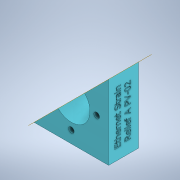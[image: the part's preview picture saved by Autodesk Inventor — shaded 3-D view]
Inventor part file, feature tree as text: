
AUTODESK INVENTOR PART (.ipt)
format: ipt  version: 2022.1 (Build 261234000, 234)  size: 969,216 bytes
history: native  units: mm
features: sketch x7, extrude x2, revolve x2, emboss x2, hole x1, plane x1, split x1
ambient origin geometry x8: Origin, YZ Plane, XZ Plane, XY Plane, X Axis, Y Axis, Z Axis, Center Point
bodies: Solid7 (feature_tree)
feature tree (16):
  extrude  "Extrusion20"  Depth=50.0mm
  revolve  "Revolution4"  [1 undecoded]
  extrude  "Extrusion21"  TaperAngle=90.0deg  [1 undecoded]
  revolve  "Revolution5"  [1 undecoded]
  hole  "Hole2"  [1 undecoded]
  plane  "Work Plane6"
  emboss  "Emboss3"
  emboss  "Emboss4"
  split  "Split1"
  sketch  "Sketch27"  dims[d124=50.0mm d125=50.0mm]
  sketch  "Sketch28"  dims[d126=15.0mm d127=0.0mm d128=3.0mm]
  sketch  "Sketch29"  dims[d129=12.5mm d130=90.0deg]
  sketch  "Sketch30"  dims[d131=5.0mm d132=0.0mm d133=2.5mm]
  sketch  "Sketch31"  dims[d134=90.0deg d135=34.0mm]
  sketch  "Sketch32"  dims[d136=34.0mm]
  sketch  "Sketch33"  dims[d137=3.81mm d138=6.0mm d139=8.89mm d140=3.145mm d141=14.3117mm d142=8.0mm d143=20.594885mm d144=1.0mm d145=0.0mm d146=1.0mm d147=0.0mm]
note: 4 required parameter values undecoded (feature->parameter linkage not recoverable at this tier; creation-order binding heuristic only, values carry confidence <= 0.55)